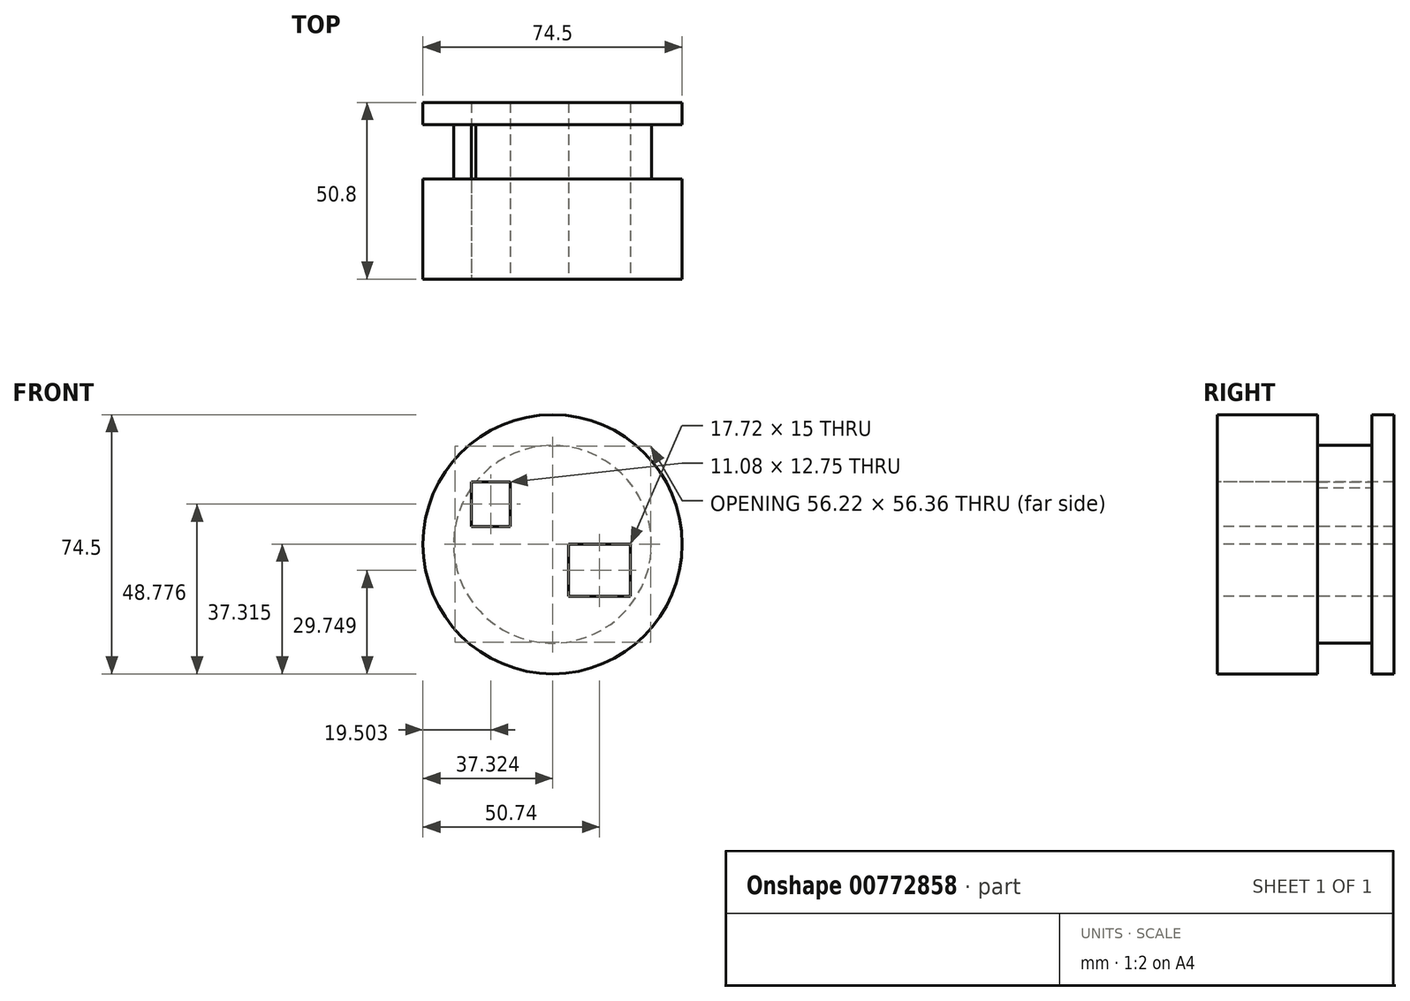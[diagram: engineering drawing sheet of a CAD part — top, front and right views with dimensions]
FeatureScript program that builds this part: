
annotation { "Feature Type Name" : "Feature", "Feature Type Description" : "" }
export const myFeature = defineFeature(function(context is Context, id is Id, definition is map)
    precondition{}
    {
        {
            var Q0;
            Q0=qCreatedBy(makeId("Front.planeOp"),FACE);
            var sketch = newSketch(context, id + "F0", { "sketchPlane" : qUnion([Q0])});
            skCircle(sketch, "E0", {"center": v(0, 0) * mm, "radius": 37.25 * mm});
            skSolve(sketch);
        }
        {
            var Q0;
            Q0=makeQuery(id+"F0.imprint","IMPRINT",FACE,{"disambiguationData":[TD([[makeQuery(id+"F0.imprint","IMPRINT",EDGE,{"derivedFrom":sQuery(id+"F0.wireOp",EDGE,"E0")}),1.0]])]});
            extrude(context, id + "F1", {"entities" : qUnion([Q0]), "depth" : 50.8 * mm, "offsetDistance" : 25.4 * mm});
        }
        {
            var Q0;
            Q0=makeQuery(id+"F1.opExtrude","CAP_FACE",FACE,{"disambiguationData":[OSD([sQuery(id+"F0.wireOp",EDGE,"E0")])],"isStart":false});
            var sketch = newSketch(context, id + "F2", { "sketchPlane" : qUnion([Q0])});
            skLineSegment(sketch, "E1.bottom", {"start": v(-23.29, 17.9) * mm, "end": v(-12.2, 17.9) * mm});
            skLineSegment(sketch, "E1.top", {"start": v(-23.29, 5.15) * mm, "end": v(-12.2, 5.15) * mm});
            skLineSegment(sketch, "E1.left", {"start": v(-23.29, 17.9) * mm, "end": v(-23.29, 5.15) * mm});
            skLineSegment(sketch, "E1.right", {"start": v(-12.2, 17.9) * mm, "end": v(-12.2, 5.15) * mm});
            skLineSegment(sketch, "E2.bottom", {"start": v(4.63, 0) * mm, "end": v(22.35, 0) * mm});
            skLineSegment(sketch, "E2.top", {"start": v(4.63, -15) * mm, "end": v(22.35, -15) * mm});
            skLineSegment(sketch, "E2.left", {"start": v(4.63, 0) * mm, "end": v(4.63, -15) * mm});
            skLineSegment(sketch, "E2.right", {"start": v(22.35, 0) * mm, "end": v(22.35, -15) * mm});
            skSolve(sketch);
        }
        {
            var Q0;
            Q0 = qSketchRegion(id + "F2", true);
            extrude(context, id + "F3", {"entities" : qUnion([Q0]), "operationType" : NewBodyOperationType.REMOVE, "oppositeDirection" : true, "depth" : 50.8 * mm, "offsetDistance" : 25.4 * mm});
        }
        {
            var Q0;
            Q0=qCreatedBy(makeId("Top.planeOp"),FACE);
            var sketch = newSketch(context, id + "F4", { "sketchPlane" : qUnion([Q0])});
            skLineSegment(sketch, "E3", {"start": v(0, 0) * mm, "end": v(0, 32.76) * mm, "construction": true});
            skLineSegment(sketch, "E4.bottom", {"start": v(-42.3, -6.38) * mm, "end": v(-28.42, -6.38) * mm});
            skLineSegment(sketch, "E4.top", {"start": v(-42.3, -21.98) * mm, "end": v(-28.42, -21.98) * mm});
            skLineSegment(sketch, "E4.left", {"start": v(-42.3, -6.38) * mm, "end": v(-42.3, -21.98) * mm});
            skLineSegment(sketch, "E4.right", {"start": v(-28.42, -6.38) * mm, "end": v(-28.42, -21.98) * mm});
            skSolve(sketch);
        }
        {
            var Q0;
            Q0=qCreatedBy(makeId("Top.planeOp"),FACE);
            var sketch = newSketch(context, id + "F5", { "sketchPlane" : qUnion([Q0])});
            skLineSegment(sketch, "E5", {"start": v(0, 0) * mm, "end": v(0, 37.7) * mm});
            skSolve(sketch);
        }
        {
            var Q0;
            Q0 = qSketchRegion(id + "F4", true);
            var Q1;
            Q1=sQuery(id+"F5.wireOp",EDGE,"E5");
            revolve(context, id + "F6", {"operationType" : NewBodyOperationType.REMOVE, "surfaceOperationType" : NewSurfaceOperationType.NEW, "entities" : qUnion([Q0]), "axis" : qUnion([Q1]), "revolveType" : RevolveType.FULL, "oppositeDirection" : true});
        }
    });
